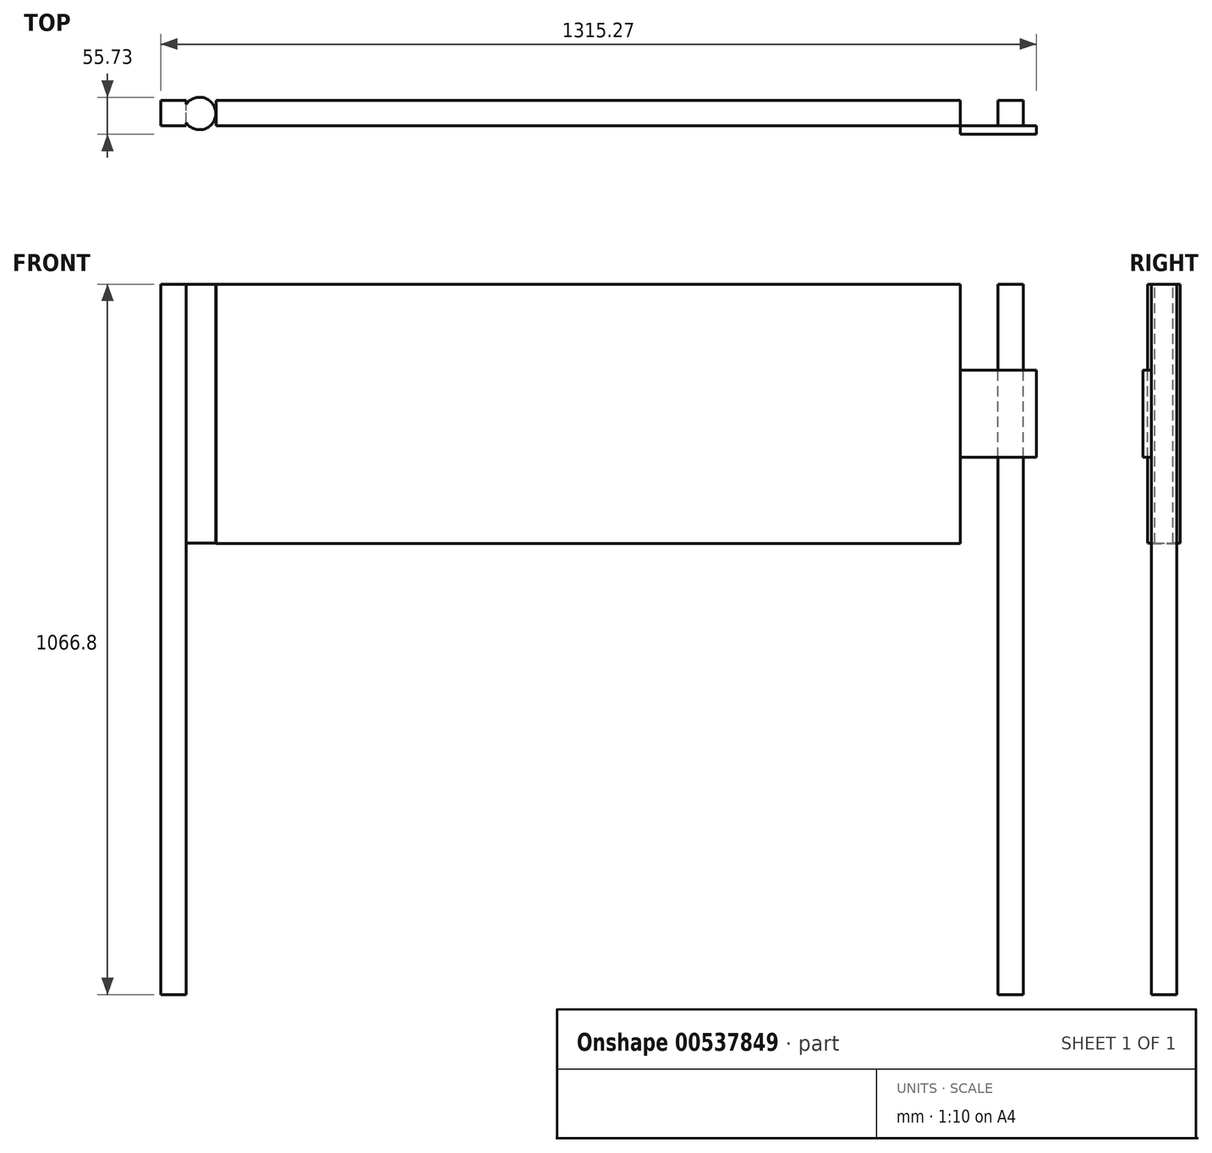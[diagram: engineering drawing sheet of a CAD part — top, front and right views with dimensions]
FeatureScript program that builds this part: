
annotation { "Feature Type Name" : "Feature", "Feature Type Description" : "" }
export const myFeature = defineFeature(function(context is Context, id is Id, definition is map)
    precondition{}
    {
        {
            var Q0;
            Q0=qCreatedBy(makeId("Front.planeOp"),FACE);
            var sketch = newSketch(context, id + "F0", { "sketchPlane" : qUnion([Q0])});
            skLineSegment(sketch, "E0.bottom", {"start": v(596.6, 0) * mm, "end": v(634.7, 0) * mm});
            skLineSegment(sketch, "E0.top", {"start": v(596.6, 1066.8) * mm, "end": v(634.7, 1066.8) * mm});
            skLineSegment(sketch, "E0.left", {"start": v(596.6, 0) * mm, "end": v(596.6, 1066.8) * mm});
            skLineSegment(sketch, "E0.right", {"start": v(634.7, 0) * mm, "end": v(634.7, 1066.8) * mm});
            skLineSegment(sketch, "E1", {"start": v(596.6, 0) * mm, "end": v(-622.6, 0) * mm});
            skLineSegment(sketch, "E2.bottom", {"start": v(-622.6, 0) * mm, "end": v(-660.7, 0) * mm});
            skLineSegment(sketch, "E2.top", {"start": v(-622.6, 1066.8) * mm, "end": v(-660.7, 1066.8) * mm});
            skLineSegment(sketch, "E2.left", {"start": v(-622.6, 0) * mm, "end": v(-622.6, 1066.8) * mm});
            skLineSegment(sketch, "E2.right", {"start": v(-660.7, 0) * mm, "end": v(-660.7, 1066.8) * mm});
            skLineSegment(sketch, "E3.bottom", {"start": v(540.27, 1066.8) * mm, "end": v(-577.33, 1066.8) * mm});
            skLineSegment(sketch, "E3.top", {"start": v(540.27, 677.13) * mm, "end": v(-577.33, 677.13) * mm});
            skLineSegment(sketch, "E3.left", {"start": v(540.27, 1066.8) * mm, "end": v(540.27, 677.13) * mm});
            skLineSegment(sketch, "E3.right", {"start": v(-577.33, 1066.8) * mm, "end": v(-577.33, 677.13) * mm});
            skSolve(sketch);
        }
        {
            var Q0;
            Q0 = qSketchRegion(id + "F0", true);
            extrude(context, id + "F1", {"entities" : qUnion([Q0]), "depth" : 38.1 * mm, "offsetDistance" : 25.4 * mm});
        }
        {
            var Q0;
            Q0=makeQuery(id+"F1.opExtrude","SWEPT_FACE",FACE,{"disambiguationData":[OSD([sQuery(id+"F0.wireOp",EDGE,"E2.top")])]});
            var sketch = newSketch(context, id + "F2", { "sketchPlane" : qUnion([Q0])});
            skCircle(sketch, "E4", {"center": v(-602.4, -19.52) * mm, "radius": 24.45 * mm});
            skSolve(sketch);
        }
        {
            var Q0;
            {var subQ0=sQuery(id+"F2.wireOp",EDGE,"E4");var subQ1=makeQuery(id+"F1.opExtrude","SWEPT_EDGE",EDGE,{"disambiguationData":[OSD([sQuery(id+"F0.wireOp",EDGE,"E2.top"),sQuery(id+"F0.wireOp",EDGE,"E2.left")])]});var subQ2=makeQuery(id+"F2.imprint","INTERSECT",VERTEX,{"disambiguationData":[OD(0.0)],"derivedFrom":[subQ1,subQ0]});Q0=makeQuery(id+"F2.imprint","IMPRINT",FACE,{"disambiguationData":[TD([[makeQuery(id+"F2.imprint","IMPRINT",EDGE,{"disambiguationData":[TD([[subQ2,1.0]])],"derivedFrom":subQ0}),1.0]])]});}
            extrude(context, id + "F3", {"entities" : qUnion([Q0]), "operationType" : NewBodyOperationType.ADD, "oppositeDirection" : true, "depth" : 388.62 * mm, "offsetDistance" : 25.4 * mm});
        }
        {
            var Q0;
            Q0=makeQuery(id+"F1.opExtrude","CAP_FACE",FACE,{"disambiguationData":[OSD([sQuery(id+"F0.wireOp",EDGE,"E3.bottom"),sQuery(id+"F0.wireOp",EDGE,"E3.top"),sQuery(id+"F0.wireOp",EDGE,"E3.left"),sQuery(id+"F0.wireOp",EDGE,"E3.right")])],"isStart":false});
            var sketch = newSketch(context, id + "F4", { "sketchPlane" : qUnion([Q0])});
            skLineSegment(sketch, "E5", {"start": v(654.58, 871.96) * mm, "end": v(654.58, 937.4) * mm});
            skLineSegment(sketch, "E6", {"start": v(654.58, 937.4) * mm, "end": v(540.27, 937.4) * mm});
            skLineSegment(sketch, "E7", {"start": v(540.27, 937.4) * mm, "end": v(540.27, 871.96) * mm});
            skLineSegment(sketch, "E8.MirrorCS", {"start": v(540.27, 806.53) * mm, "end": v(540.27, 871.96) * mm});
            skLineSegment(sketch, "E9.MirrorCS", {"start": v(654.58, 871.96) * mm, "end": v(654.58, 806.53) * mm});
            skLineSegment(sketch, "E10.MirrorCS", {"start": v(654.58, 806.53) * mm, "end": v(540.27, 806.53) * mm});
            skSolve(sketch);
        }
        {
            var Q0;
            Q0=makeQuery(id+"F4.imprint","IMPRINT",FACE,{"disambiguationData":[TD([[makeQuery(id+"F4.imprint","IMPRINT",EDGE,{"derivedFrom":sQuery(id+"F4.wireOp",EDGE,"E5")}),1.0]])]});
            extrude(context, id + "F5", {"entities" : qUnion([Q0]), "operationType" : NewBodyOperationType.ADD, "depth" : 12.7 * mm, "offsetDistance" : 25.4 * mm});
        }
    });
